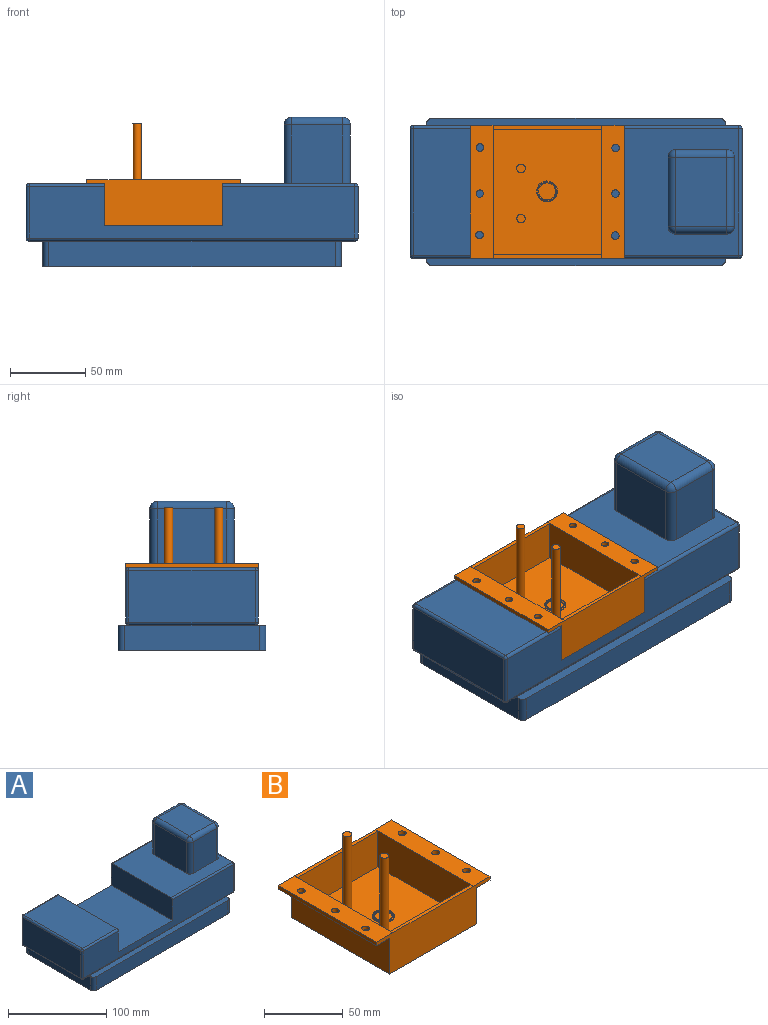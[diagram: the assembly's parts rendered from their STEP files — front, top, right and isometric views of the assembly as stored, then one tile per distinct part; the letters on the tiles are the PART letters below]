
ASSEMBLY  parts=2 mates=1
PART A: 61 faces, bbox 220x98x99 mm
  f0: plane 198x7mm, normal (0,0,1), area 1379.1mm2, adj f2,f3,f4,f7,f8,f37
  f1: plane 198x7mm, normal (0,0,1), area 1379.1mm2, adj f2,f4,f5,f9,f10,f29
  f2: plane 90x17mm, normal (-1,0,0), area 1530mm2, adj f0,f1,f6,f7,f10,f11
  f3: plane 190x17mm, normal (0,-1,0), area 3230mm2, adj f0,f6,f7,f8
  f4: plane 90x17mm, normal (1,0,0), area 1530mm2, adj f0,f1,f6,f8,f9,f18
  f5: plane 190x17mm, normal (0,1,0), area 3230mm2, adj f1,f6,f9,f10
  f6: plane 198x98mm, normal (0,0,-1), area 19390.3mm2, adj f2,f3,f4,f5,f7,f8,f9,f10
  f7: cylinder r=4mm len=17mm, axis (0,0,-1), area 106.8mm2, adj f0,f2,f3,f6
  f8: cylinder r=4mm len=17mm, axis (0,0,1), area 106.8mm2, adj f0,f3,f4,f6
  f9: cylinder r=4mm len=17mm, axis (0,0,-1), area 106.8mm2, adj f1,f4,f5,f6
  f10: cylinder r=4mm len=17mm, axis (0,0,1), area 106.8mm2, adj f1,f2,f5,f6
  f11: plane 84x9mm, normal (0,0,-1), area 756mm2, adj f2,f29,f30,f37
  f12: plane 88x84mm, normal (0,0,1), area 4949.5mm2, adj f19,f34,f40,f43,f44,f45,f46,f47
  f13: plane 216x34mm, normal (0,-1,0), area 5316mm2, adj f19,f20,f21,f26,f31,f37,f41,f43
  f14: plane 216x34mm, normal (0,1,0), area 5316mm2, adj f19,f20,f21,f22,f24,f29,f34,f35
  f15: plane 84x34mm, normal (-1,0,0), area 2856mm2, adj f24,f25,f30,f31
  f16: plane 84x34mm, normal (1,0,0), area 2856mm2, adj f35,f36,f40,f41
  f17: plane 84x50mm, normal (0,0,1), area 4200mm2, adj f20,f22,f25,f26
  f18: plane 84x9mm, normal (0,0,-1), area 756mm2, adj f4,f29,f36,f37
  f19: plane 88x28mm, normal (-1,0,0), area 2462.3mm2, adj f12,f13,f14,f21,f34,f43
  f20: plane 88x28mm, normal (1,0,0), area 2462.3mm2, adj f13,f14,f17,f21,f22,f26
  f21: plane 88x78mm, normal (0,0,1), area 6864mm2, adj f13,f14,f19,f20
  f22: cylinder r=2mm len=50mm, axis (1,0,0), area 157.1mm2, adj f14,f17,f20,f23
  f23: sphere r=2mm, area 6.3mm2, adj f22,f24,f25
  f24: cylinder r=2mm len=34mm, axis (0,0,1), area 106.8mm2, adj f14,f15,f23,f27
  f25: cylinder r=2mm len=84mm, axis (0,1,0), area 263.9mm2, adj f15,f17,f23,f28
  f26: cylinder r=2mm len=50mm, axis (-1,0,0), area 157.1mm2, adj f13,f17,f20,f28
  f27: sphere r=2mm, area 6.3mm2, adj f24,f29,f30
  f28: sphere r=2mm, area 6.3mm2, adj f25,f26,f31
  f29: cylinder r=2mm len=216mm, axis (-1,0,0), area 678.6mm2, adj f1,f11,f14,f18,f27,f32
  f30: cylinder r=2mm len=84mm, axis (0,-1,0), area 263.9mm2, adj f11,f15,f27,f33
  f31: cylinder r=2mm len=34mm, axis (0,0,-1), area 106.8mm2, adj f13,f15,f28,f33
  f32: sphere r=2mm, area 6.3mm2, adj f29,f35,f36
  f33: sphere r=2mm, area 6.3mm2, adj f30,f31,f37
  f34: cylinder r=2mm len=88mm, axis (1,0,0), area 276.5mm2, adj f12,f14,f19,f38
  f35: cylinder r=2mm len=34mm, axis (0,0,-1), area 106.8mm2, adj f14,f16,f32,f38
  f36: cylinder r=2mm len=84mm, axis (0,1,0), area 263.9mm2, adj f16,f18,f32,f39
  f37: cylinder r=2mm len=216mm, axis (1,0,0), area 678.6mm2, adj f0,f11,f13,f18,f33,f39
  f38: sphere r=2mm, area 6.3mm2, adj f34,f35,f40
  f39: sphere r=2mm, area 6.3mm2, adj f36,f37,f41
  f40: cylinder r=2mm len=84mm, axis (0,-1,0), area 263.9mm2, adj f12,f16,f38,f42
  f41: cylinder r=2mm len=34mm, axis (0,0,1), area 106.8mm2, adj f13,f16,f39,f42
  f42: sphere r=2mm, area 6.3mm2, adj f40,f41,f43
  f43: cylinder r=2mm len=88mm, axis (-1,0,0), area 276.5mm2, adj f12,f13,f19,f42
  f44: plane 39x34mm, normal (0,-1,0), area 1326mm2, adj f12,f51,f57,f60
  f45: plane 46x39mm, normal (1,0,0), area 1794mm2, adj f12,f54,f58,f60
  f46: plane 39x34mm, normal (0,1,0), area 1326mm2, adj f12,f49,f53,f54
  f47: plane 46x39mm, normal (-1,0,0), area 1794mm2, adj f12,f49,f51,f52
  f48: plane 46x34mm, normal (0,0,1), area 1564mm2, adj f52,f53,f57,f58
  f49: cylinder r=5mm len=39mm, axis (0,0,-1), area 306.3mm2, adj f12,f46,f47,f50
  f50: sphere r=5mm, area 39.3mm2, adj f49,f52,f53
  f51: cylinder r=5mm len=39mm, axis (0,0,1), area 306.3mm2, adj f12,f44,f47,f55
  f52: cylinder r=5mm len=46mm, axis (0,1,0), area 361.3mm2, adj f47,f48,f50,f55
  f53: cylinder r=5mm len=34mm, axis (1,0,0), area 267mm2, adj f46,f48,f50,f56
  f54: cylinder r=5mm len=39mm, axis (0,0,1), area 306.3mm2, adj f12,f45,f46,f56
  f55: sphere r=5mm, area 39.3mm2, adj f51,f52,f57
  f56: sphere r=5mm, area 39.3mm2, adj f53,f54,f58
  f57: cylinder r=5mm len=34mm, axis (-1,0,0), area 267mm2, adj f44,f48,f55,f59
  f58: cylinder r=5mm len=46mm, axis (0,-1,0), area 361.3mm2, adj f45,f48,f56,f59
  f59: sphere r=5mm, area 39.3mm2, adj f57,f58,f60
  f60: cylinder r=5mm len=39mm, axis (0,0,-1), area 306.3mm2, adj f12,f44,f45,f59
PART B: 34 faces, bbox 102x88x68 mm
  f0: plane 88x27.75mm, normal (-1,0,0), area 2307.8mm2, adj f1,f11,f12,f13,f20,f21,f22,f23
  f1: plane 83.14x72mm, normal (0,0,1), area 5786.1mm2, adj f0,f2,f20,f22,f24,f30,f32
  f2: plane 88x27.75mm, normal (1,0,0), area 2307.8mm2, adj f1,f3,f12,f13,f20,f21,f22,f23
  f3: plane 88x15mm, normal (0,0,1), area 1262.2mm2, adj f2,f4,f12,f13,f17,f18,f19
  f4: plane 88x2.75mm, normal (-1,0,0), area 241.9mm2, adj f3,f5,f12,f13
  f5: plane 88x12mm, normal (0,0,-1), area 998.1mm2, adj f4,f6,f12,f13,f17,f18,f19
  f6: plane 88x28mm, normal (-1,0,0), area 2464mm2, adj f5,f7,f12,f13
  f7: plane 88x78mm, normal (0,0,-1), area 6864mm2, adj f6,f8,f12,f13
  f8: plane 88x28mm, normal (1,0,0), area 2464mm2, adj f7,f9,f12,f13
  f9: plane 88x12mm, normal (0,0,-1), area 997.4mm2, adj f8,f10,f12,f13,f14,f15,f16
  f10: plane 88x2.75mm, normal (1,0,0), area 241.9mm2, adj f9,f11,f12,f13
  f11: plane 88x15mm, normal (0,0,1), area 1261.5mm2, adj f0,f10,f12,f13,f14,f15,f16
  f12: plane 102x30.75mm, normal (0,-1,0), area 2453.6mm2, adj f0,f2,f3,f4,f5,f6,f7,f8
  f13: plane 102x30.75mm, normal (0,1,0), area 2453.6mm2, adj f0,f2,f3,f4,f5,f6,f7,f8
  f14: cylinder r=2.47mm len=4.95mm, axis (0,0,1), area 42.7mm2, adj f9,f11
  f15: cylinder r=2.5mm len=5mm, axis (0,0,1), area 43.2mm2, adj f9,f11
  f16: cylinder r=2.5mm len=5mm, axis (0,0,1), area 43.2mm2, adj f9,f11
  f17: cylinder r=2.5mm len=5mm, axis (0,0,1), area 43.2mm2, adj f3,f5
  f18: cylinder r=2.43mm len=4.86mm, axis (0,0,1), area 41.9mm2, adj f3,f5
  f19: cylinder r=2.5mm len=5mm, axis (0,0,1), area 43.2mm2, adj f3,f5
  f20: plane 72x27.6mm, normal (0,-1,0), area 1987.1mm2, adj f0,f1,f2,f21
  f21: plane 72x2.49mm, normal (0,0,1), area 179.3mm2, adj f0,f2,f13,f20
  f22: plane 72x27.6mm, normal (0,1,0), area 1987.1mm2, adj f0,f1,f2,f23
  f23: plane 72x2.37mm, normal (0,0,1), area 170.4mm2, adj f0,f2,f12,f22
  f24: cylinder r=6.92mm len=13.84mm, axis (0,0,-1), area 21.7mm2, adj f1,f29
  f25: plane 12.84x12.84mm, normal (0,0,1), area 11.6mm2, adj f28,f29
  f26: cylinder r=5.63mm len=11.25mm, axis (0,0,1), area 17.7mm2, adj f27,f28
  f27: plane 11.25x11.25mm, normal (0,0,1), area 99.5mm2, adj f26
  f28: torus R=6.13mm, axis (0,0,1), area 28.7mm2, adj f25,f26
  f29: torus R=6.42mm, axis (0,0,1), area 33.3mm2, adj f24,f25
  f30: cylinder r=2.83mm len=65mm, axis (0,0,-1), area 1157.6mm2, adj f1,f31
  f31: plane 5.67x5.67mm, normal (0,0,1), area 25.2mm2, adj f30
  f32: cylinder r=2.79mm len=65mm, axis (0,0,-1), area 1137.8mm2, adj f1,f33
  f33: plane 5.57x5.57mm, normal (0,0,1), area 24.4mm2, adj f32
PLACE A t=(0,0,0.25)mm
PLACE B t=(-6.02,-4.81,36.88)mm
MATE fastened B.f7 <-> A.f21  axis (0,0,1) through (-8.99,-4.81,27.25)mm
